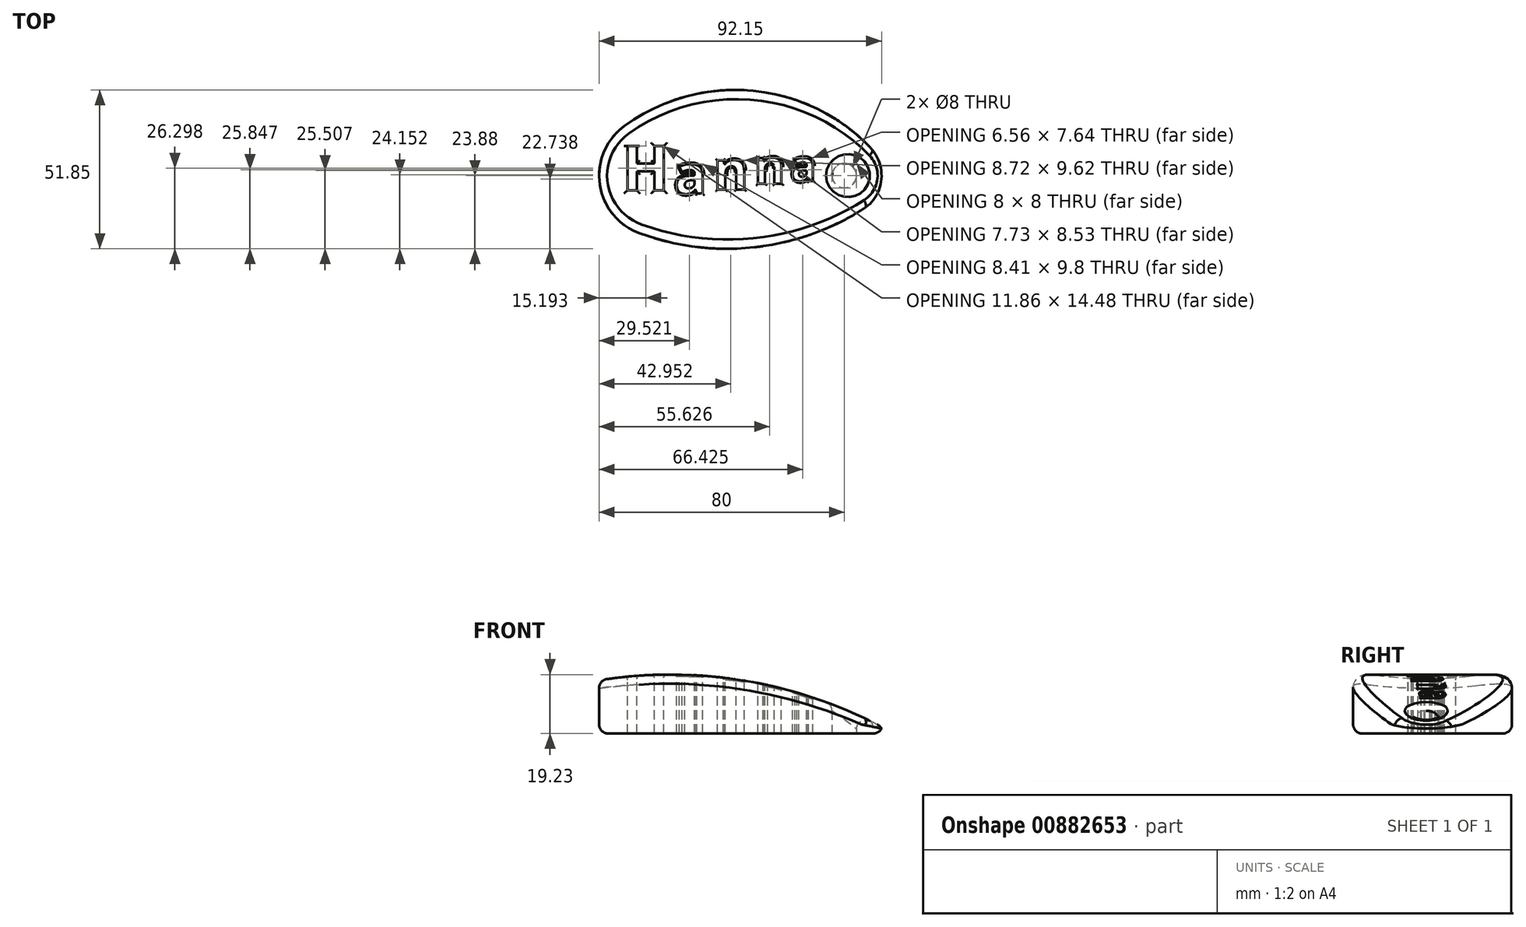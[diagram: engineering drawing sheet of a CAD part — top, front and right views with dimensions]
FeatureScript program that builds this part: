
annotation { "Feature Type Name" : "Feature", "Feature Type Description" : "" }
export const myFeature = defineFeature(function(context is Context, id is Id, definition is map)
    precondition{}
    {
        {
            var Q0;
            Q0=qCreatedBy(makeId("Top.planeOp"),FACE);
            var sketch = newSketch(context, id + "F0", { "sketchPlane" : qUnion([Q0])});
            skLineSegment(sketch, "E0", {"start": v(0, 0) * mm, "end": v(-60, 0) * mm});
            skCircle(sketch, "E1", {"center": v(0, 0) * mm, "radius": 12.5 * mm});
            skCircle(sketch, "E2", {"center": v(-60, 0) * mm, "radius": 20 * mm});
            skCircle(sketch, "E3", {"center": v(-35.63, -33.3) * mm, "radius": 61.27 * mm});
            skCircle(sketch, "E4", {"center": v(-38.3, 58.71) * mm, "radius": 82.6 * mm});
            skCircle(sketch, "E5", {"center": v(0, 0) * mm, "radius": 4 * mm});
            skSolve(sketch);
        }
        {
            var Q0;
            {var subQ0=sQuery(id+"F0.wireOp",EDGE,"E2");var subQ1=makeQuery(id+"F0.imprint","INTERSECT",VERTEX,{"derivedFrom":[sQuery(id+"F0.wireOp",EDGE,"E0"),subQ0]});Q0=makeQuery(id+"F0.imprint","IMPRINT",FACE,{"disambiguationData":[TD([[makeQuery(id+"F0.imprint","IMPRINT",EDGE,{"disambiguationData":[TD([[subQ1,-1.0]])],"derivedFrom":subQ0}),1.0]])]});}
            var Q1;
            {var subQ0=sQuery(id+"F0.wireOp",EDGE,"E1");var subQ1=sQuery(id+"F0.wireOp",EDGE,"E0");var subQ2=makeQuery(id+"F0.imprint","INTERSECT",VERTEX,{"derivedFrom":[subQ1,subQ0]});Q1=makeQuery(id+"F0.imprint","IMPRINT",FACE,{"disambiguationData":[TD([[makeQuery(id+"F0.imprint","IMPRINT",EDGE,{"disambiguationData":[TD([[subQ2,-1.0]])],"derivedFrom":subQ1}),-1.0]])]});}
            var Q2;
            Q2=makeQuery(id+"F0.imprint","IMPRINT",FACE,{"disambiguationData":[TD([[makeQuery(id+"F0.imprint","IMPRINT",EDGE,{"derivedFrom":sQuery(id+"F0.wireOp",EDGE,"E5")}),-1.0]])]});
            var Q3;
            {var subQ0=sQuery(id+"F0.wireOp",EDGE,"E1");var subQ1=sQuery(id+"F0.wireOp",EDGE,"E0");var subQ2=makeQuery(id+"F0.imprint","INTERSECT",VERTEX,{"derivedFrom":[subQ1,subQ0]});Q3=makeQuery(id+"F0.imprint","IMPRINT",FACE,{"disambiguationData":[TD([[makeQuery(id+"F0.imprint","IMPRINT",EDGE,{"disambiguationData":[TD([[subQ2,-1.0]])],"derivedFrom":subQ1}),1.0]])]});}
            extrude(context, id + "F1", {"entities" : qUnion([Q0, Q1, Q2, Q3]), "depth" : 20 * mm, "offsetDistance" : 25 * mm});
        }
        {
            var Q0;
            Q0=makeQuery(id+"F1.opExtrude","CAP_FACE",FACE,{"disambiguationData":[OSD([sQuery(id+"F0.wireOp",EDGE,"E1"),sQuery(id+"F0.wireOp",EDGE,"E2"),sQuery(id+"F0.wireOp",EDGE,"E3"),sQuery(id+"F0.wireOp",EDGE,"E4"),sQuery(id+"F0.wireOp",EDGE,"E5")])],"isStart":false});
            var sketch = newSketch(context, id + "F2", { "sketchPlane" : qUnion([Q0])});
            skText(sketch, "E6", { "text": "H", "fontName": "OpenSans-Bold.ttf"});
            skText(sketch, "E7", { "text": "a", "fontName": "OpenSans-Bold.ttf"});
            skText(sketch, "E8", { "text": "n", "fontName": "OpenSans-Bold.ttf"});
            skText(sketch, "E9", { "text": "n", "fontName": "OpenSans-Bold.ttf"});
            skText(sketch, "E10", { "text": "a", "fontName": "OpenSans-Bold.ttf"});
            const initialGuessF2  = {"E6": [-0.07256, -0.00482, 1, 0, 0.0146], "E7": [-0.05541, -0.00587, 1, 0, 0.01244], "E8": [-0.02944, -0.00264, 1, 0, 0.01105], "E9": [-0.04276, -0.00454, 1, 0, 0.01246], "E10": [-0.01742, -0.00172, 1, 0, 0.0097]};
            skSetInitialGuess(sketch, initialGuessF2);
            skSolve(sketch);
        }
        {
            var Q0;
            Q0 = qSketchRegion(id + "F2", true);
            extrude(context, id + "F3", {"entities" : qUnion([Q0]), "operationType" : NewBodyOperationType.REMOVE, "endBound" : BoundingType.THROUGH_ALL, "oppositeDirection" : true, "depth" : 25 * mm, "offsetDistance" : 25 * mm});
        }
        {
            var Q0;
            Q0=qCreatedBy(makeId("Front.planeOp"),FACE);
            cPlane(context, id + "F4", {"entities" : qUnion([Q0]), "cplaneType" : CPlaneType.OFFSET, "offset" : 40 * mm, "width" : 150 * mm, "height" : 150 * mm});
        }
        {
            var Q0;
            Q0=qCreatedBy(id+"F4.planeOp",FACE);
            var sketch = newSketch(context, id + "F5", { "sketchPlane" : qUnion([Q0])});
            skLineSegment(sketch, "E11", {"start": v(-203.83, 59.63) * mm, "end": v(87.32, 59.63) * mm});
            skLineSegment(sketch, "E12", {"start": v(87.32, 59.63) * mm, "end": v(87.32, -96.28) * mm});
            skLineSegment(sketch, "E13", {"start": v(-203.83, 59.63) * mm, "end": v(-203.83, -138.54) * mm});
            skCircle(sketch, "E14", {"center": v(-56.68, -128.28) * mm, "radius": 147.51 * mm});
            skSolve(sketch);
        }
        {
            var Q0;
            Q0=makeQuery(id+"F5.imprint","IMPRINT",FACE,{"disambiguationData":[TD([[makeQuery(id+"F5.imprint","IMPRINT",EDGE,{"derivedFrom":sQuery(id+"F5.wireOp",EDGE,"E11")}),-1.0]])]});
            extrude(context, id + "F6", {"entities" : qUnion([Q0]), "operationType" : NewBodyOperationType.REMOVE, "endBound" : BoundingType.THROUGH_ALL, "oppositeDirection" : true, "depth" : 25 * mm, "offsetDistance" : 25 * mm});
        }
        {
            var Q0;
            Q0=makeQuery(id+"F6.boolean.opBoolean","INTERSECT",EDGE,{"derivedFrom":[makeQuery(id+"F1.opExtrude","SWEPT_FACE",FACE,{"disambiguationData":[OSD([sQuery(id+"F0.wireOp",EDGE,"E4")])]}),makeQuery(id+"F6.opExtrude","SWEPT_FACE",FACE,{"disambiguationData":[OSD([sQuery(id+"F5.wireOp",EDGE,"E14")])]})]});
            var Q1;
            Q1=makeQuery(id+"F6.boolean.opBoolean","INTERSECT",EDGE,{"derivedFrom":[makeQuery(id+"F1.opExtrude","SWEPT_FACE",FACE,{"disambiguationData":[OSD([sQuery(id+"F0.wireOp",EDGE,"E5")])]}),makeQuery(id+"F6.opExtrude","SWEPT_FACE",FACE,{"disambiguationData":[OSD([sQuery(id+"F5.wireOp",EDGE,"E14")])]})]});
            var Q2;
            Q2=makeQuery(id+"F1.opExtrude","CAP_EDGE",EDGE,{"disambiguationData":[OSD([sQuery(id+"F0.wireOp",EDGE,"E3")])],"isStart":true});
            fillet(context, id + "F7", {"entities" : qUnion([Q0, Q1, Q2]), "radius" : 3 * mm, "tangentPropagation" : true, "allowEdgeOverflow" : false});
        }
        {
            var Q0;
            Q0=makeQuery(id+"F6.boolean.opBoolean","INTERSECT",EDGE,{"derivedFrom":[makeQuery(id+"F3.boolean.opBoolean","COPY",FACE,{"derivedFrom":makeQuery(id+"F3.opExtrude","SWEPT_FACE",FACE,{"disambiguationData":[OSD([sQuery(id+"F2.wireOp",EDGE,"E6.sketch_text.stroke-7")])]})}),makeQuery(id+"F6.opExtrude","SWEPT_FACE",FACE,{"disambiguationData":[OSD([sQuery(id+"F5.wireOp",EDGE,"E14")])]})]});
            var Q1;
            Q1=makeQuery(id+"F6.boolean.opBoolean","INTERSECT",EDGE,{"derivedFrom":[makeQuery(id+"F3.boolean.opBoolean","COPY",FACE,{"derivedFrom":makeQuery(id+"F3.opExtrude","SWEPT_FACE",FACE,{"disambiguationData":[OSD([sQuery(id+"F2.wireOp",EDGE,"E6.sketch_text.stroke-8")])]})}),makeQuery(id+"F6.opExtrude","SWEPT_FACE",FACE,{"disambiguationData":[OSD([sQuery(id+"F5.wireOp",EDGE,"E14")])]})]});
            var Q2;
            Q2=makeQuery(id+"F6.boolean.opBoolean","INTERSECT",EDGE,{"derivedFrom":[makeQuery(id+"F3.boolean.opBoolean","COPY",FACE,{"derivedFrom":makeQuery(id+"F3.opExtrude","SWEPT_FACE",FACE,{"disambiguationData":[OSD([sQuery(id+"F2.wireOp",EDGE,"E6.sketch_text.stroke-9")])]})}),makeQuery(id+"F6.opExtrude","SWEPT_FACE",FACE,{"disambiguationData":[OSD([sQuery(id+"F5.wireOp",EDGE,"E14")])]})]});
            var Q3;
            Q3=makeQuery(id+"F6.boolean.opBoolean","INTERSECT",EDGE,{"derivedFrom":[makeQuery(id+"F3.boolean.opBoolean","COPY",FACE,{"derivedFrom":makeQuery(id+"F3.opExtrude","SWEPT_FACE",FACE,{"disambiguationData":[OSD([sQuery(id+"F2.wireOp",EDGE,"E6.sketch_text.stroke-10")])]})}),makeQuery(id+"F6.opExtrude","SWEPT_FACE",FACE,{"disambiguationData":[OSD([sQuery(id+"F5.wireOp",EDGE,"E14")])]})]});
            var Q4;
            Q4=makeQuery(id+"F6.boolean.opBoolean","INTERSECT",EDGE,{"derivedFrom":[makeQuery(id+"F3.boolean.opBoolean","COPY",FACE,{"derivedFrom":makeQuery(id+"F3.opExtrude","SWEPT_FACE",FACE,{"disambiguationData":[OSD([sQuery(id+"F2.wireOp",EDGE,"E6.sketch_text.stroke-11")])]})}),makeQuery(id+"F6.opExtrude","SWEPT_FACE",FACE,{"disambiguationData":[OSD([sQuery(id+"F5.wireOp",EDGE,"E14")])]})]});
            var Q5;
            Q5=makeQuery(id+"F6.boolean.opBoolean","INTERSECT",EDGE,{"derivedFrom":[makeQuery(id+"F3.boolean.opBoolean","COPY",FACE,{"derivedFrom":makeQuery(id+"F3.opExtrude","SWEPT_FACE",FACE,{"disambiguationData":[OSD([sQuery(id+"F2.wireOp",EDGE,"E6.sketch_text.stroke-0")])]})}),makeQuery(id+"F6.opExtrude","SWEPT_FACE",FACE,{"disambiguationData":[OSD([sQuery(id+"F5.wireOp",EDGE,"E14")])]})]});
            var Q6;
            Q6=makeQuery(id+"F6.boolean.opBoolean","INTERSECT",EDGE,{"derivedFrom":[makeQuery(id+"F3.boolean.opBoolean","COPY",FACE,{"derivedFrom":makeQuery(id+"F3.opExtrude","SWEPT_FACE",FACE,{"disambiguationData":[OSD([sQuery(id+"F2.wireOp",EDGE,"E6.sketch_text.stroke-1")])]})}),makeQuery(id+"F6.opExtrude","SWEPT_FACE",FACE,{"disambiguationData":[OSD([sQuery(id+"F5.wireOp",EDGE,"E14")])]})]});
            var Q7;
            Q7=makeQuery(id+"F6.boolean.opBoolean","INTERSECT",EDGE,{"derivedFrom":[makeQuery(id+"F3.boolean.opBoolean","COPY",FACE,{"derivedFrom":makeQuery(id+"F3.opExtrude","SWEPT_FACE",FACE,{"disambiguationData":[OSD([sQuery(id+"F2.wireOp",EDGE,"E6.sketch_text.stroke-2")])]})}),makeQuery(id+"F6.opExtrude","SWEPT_FACE",FACE,{"disambiguationData":[OSD([sQuery(id+"F5.wireOp",EDGE,"E14")])]})]});
            var Q8;
            Q8=makeQuery(id+"F6.boolean.opBoolean","INTERSECT",EDGE,{"derivedFrom":[makeQuery(id+"F3.boolean.opBoolean","COPY",FACE,{"derivedFrom":makeQuery(id+"F3.opExtrude","SWEPT_FACE",FACE,{"disambiguationData":[OSD([sQuery(id+"F2.wireOp",EDGE,"E6.sketch_text.stroke-3")])]})}),makeQuery(id+"F6.opExtrude","SWEPT_FACE",FACE,{"disambiguationData":[OSD([sQuery(id+"F5.wireOp",EDGE,"E14")])]})]});
            var Q9;
            Q9=makeQuery(id+"F6.boolean.opBoolean","INTERSECT",EDGE,{"derivedFrom":[makeQuery(id+"F3.boolean.opBoolean","COPY",FACE,{"derivedFrom":makeQuery(id+"F3.opExtrude","SWEPT_FACE",FACE,{"disambiguationData":[OSD([sQuery(id+"F2.wireOp",EDGE,"E6.sketch_text.stroke-5")])]})}),makeQuery(id+"F6.opExtrude","SWEPT_FACE",FACE,{"disambiguationData":[OSD([sQuery(id+"F5.wireOp",EDGE,"E14")])]})]});
            var Q10;
            Q10=makeQuery(id+"F6.boolean.opBoolean","INTERSECT",EDGE,{"derivedFrom":[makeQuery(id+"F3.boolean.opBoolean","COPY",FACE,{"derivedFrom":makeQuery(id+"F3.opExtrude","SWEPT_FACE",FACE,{"disambiguationData":[OSD([sQuery(id+"F2.wireOp",EDGE,"E6.sketch_text.stroke-4")])]})}),makeQuery(id+"F6.opExtrude","SWEPT_FACE",FACE,{"disambiguationData":[OSD([sQuery(id+"F5.wireOp",EDGE,"E14")])]})]});
            fillet(context, id + "F8", {"entities" : qUnion([Q0, Q1, Q2, Q3, Q4, Q5, Q6, Q7, Q8, Q9, Q10]), "radius" : 1 * mm, "tangentPropagation" : true, "allowEdgeOverflow" : false});
        }
        {
            var Q0;
            Q0=makeQuery(id+"F6.boolean.opBoolean","INTERSECT",EDGE,{"derivedFrom":[makeQuery(id+"F3.boolean.opBoolean","COPY",FACE,{"derivedFrom":makeQuery(id+"F3.opExtrude","SWEPT_FACE",FACE,{"disambiguationData":[OSD([sQuery(id+"F2.wireOp",EDGE,"E7.sketch_text.stroke-14")])]})}),makeQuery(id+"F6.opExtrude","SWEPT_FACE",FACE,{"disambiguationData":[OSD([sQuery(id+"F5.wireOp",EDGE,"E14")])]})]});
            var Q1;
            Q1=makeQuery(id+"F6.boolean.opBoolean","INTERSECT",EDGE,{"derivedFrom":[makeQuery(id+"F3.boolean.opBoolean","COPY",FACE,{"derivedFrom":makeQuery(id+"F3.opExtrude","SWEPT_FACE",FACE,{"disambiguationData":[OSD([sQuery(id+"F2.wireOp",EDGE,"E7.sketch_text.stroke-13")])]})}),makeQuery(id+"F6.opExtrude","SWEPT_FACE",FACE,{"disambiguationData":[OSD([sQuery(id+"F5.wireOp",EDGE,"E14")])]})]});
            var Q2;
            Q2=makeQuery(id+"F6.boolean.opBoolean","INTERSECT",EDGE,{"derivedFrom":[makeQuery(id+"F3.boolean.opBoolean","COPY",FACE,{"derivedFrom":makeQuery(id+"F3.opExtrude","SWEPT_FACE",FACE,{"disambiguationData":[OSD([sQuery(id+"F2.wireOp",EDGE,"E7.sketch_text.stroke-12")])]})}),makeQuery(id+"F6.opExtrude","SWEPT_FACE",FACE,{"disambiguationData":[OSD([sQuery(id+"F5.wireOp",EDGE,"E14")])]})]});
            var Q3;
            Q3=makeQuery(id+"F6.boolean.opBoolean","INTERSECT",EDGE,{"derivedFrom":[makeQuery(id+"F3.boolean.opBoolean","COPY",FACE,{"derivedFrom":makeQuery(id+"F3.opExtrude","SWEPT_FACE",FACE,{"disambiguationData":[OSD([sQuery(id+"F2.wireOp",EDGE,"E7.sketch_text.stroke-10")])]})}),makeQuery(id+"F6.opExtrude","SWEPT_FACE",FACE,{"disambiguationData":[OSD([sQuery(id+"F5.wireOp",EDGE,"E14")])]})]});
            var Q4;
            Q4=makeQuery(id+"F6.boolean.opBoolean","INTERSECT",EDGE,{"derivedFrom":[makeQuery(id+"F3.boolean.opBoolean","COPY",FACE,{"derivedFrom":makeQuery(id+"F3.opExtrude","SWEPT_FACE",FACE,{"disambiguationData":[OSD([sQuery(id+"F2.wireOp",EDGE,"E7.sketch_text.stroke-11")])]})}),makeQuery(id+"F6.opExtrude","SWEPT_FACE",FACE,{"disambiguationData":[OSD([sQuery(id+"F5.wireOp",EDGE,"E14")])]})]});
            var Q5;
            Q5=makeQuery(id+"F6.boolean.opBoolean","INTERSECT",EDGE,{"derivedFrom":[makeQuery(id+"F3.boolean.opBoolean","COPY",FACE,{"derivedFrom":makeQuery(id+"F3.opExtrude","SWEPT_FACE",FACE,{"disambiguationData":[OSD([sQuery(id+"F2.wireOp",EDGE,"E7.sketch_text.stroke-6")])]})}),makeQuery(id+"F6.opExtrude","SWEPT_FACE",FACE,{"disambiguationData":[OSD([sQuery(id+"F5.wireOp",EDGE,"E14")])]})]});
            var Q6;
            Q6=makeQuery(id+"F6.boolean.opBoolean","INTERSECT",EDGE,{"derivedFrom":[makeQuery(id+"F3.boolean.opBoolean","COPY",FACE,{"derivedFrom":makeQuery(id+"F3.opExtrude","SWEPT_FACE",FACE,{"disambiguationData":[OSD([sQuery(id+"F2.wireOp",EDGE,"E7.sketch_text.stroke-0")])]})}),makeQuery(id+"F6.opExtrude","SWEPT_FACE",FACE,{"disambiguationData":[OSD([sQuery(id+"F5.wireOp",EDGE,"E14")])]})]});
            var Q7;
            Q7=makeQuery(id+"F6.boolean.opBoolean","INTERSECT",EDGE,{"derivedFrom":[makeQuery(id+"F3.boolean.opBoolean","COPY",FACE,{"derivedFrom":makeQuery(id+"F3.opExtrude","SWEPT_FACE",FACE,{"disambiguationData":[OSD([sQuery(id+"F2.wireOp",EDGE,"E7.sketch_text.stroke-17")])]})}),makeQuery(id+"F6.opExtrude","SWEPT_FACE",FACE,{"disambiguationData":[OSD([sQuery(id+"F5.wireOp",EDGE,"E14")])]})]});
            fillet(context, id + "F9", {"entities" : qUnion([Q0, Q1, Q2, Q3, Q4, Q5, Q6, Q7]), "radius" : 0.5 * mm, "tangentPropagation" : true, "allowEdgeOverflow" : false});
        }
        {
            var Q0;
            Q0=makeQuery(id+"F6.boolean.opBoolean","INTERSECT",EDGE,{"derivedFrom":[makeQuery(id+"F3.boolean.opBoolean","COPY",FACE,{"derivedFrom":makeQuery(id+"F3.opExtrude","SWEPT_FACE",FACE,{"disambiguationData":[OSD([sQuery(id+"F2.wireOp",EDGE,"E7.sketch_text.stroke-8")])]})}),makeQuery(id+"F6.opExtrude","SWEPT_FACE",FACE,{"disambiguationData":[OSD([sQuery(id+"F5.wireOp",EDGE,"E14")])]})]});
            var Q1;
            Q1=makeQuery(id+"F6.boolean.opBoolean","INTERSECT",EDGE,{"derivedFrom":[makeQuery(id+"F3.boolean.opBoolean","COPY",FACE,{"derivedFrom":makeQuery(id+"F3.opExtrude","SWEPT_FACE",FACE,{"disambiguationData":[OSD([sQuery(id+"F2.wireOp",EDGE,"E9.sketch_text.stroke-8")])]})}),makeQuery(id+"F6.opExtrude","SWEPT_FACE",FACE,{"disambiguationData":[OSD([sQuery(id+"F5.wireOp",EDGE,"E14")])]})]});
            var Q2;
            Q2=makeQuery(id+"F6.boolean.opBoolean","INTERSECT",EDGE,{"derivedFrom":[makeQuery(id+"F3.boolean.opBoolean","COPY",FACE,{"derivedFrom":makeQuery(id+"F3.opExtrude","SWEPT_FACE",FACE,{"disambiguationData":[OSD([sQuery(id+"F2.wireOp",EDGE,"E9.sketch_text.stroke-9")])]})}),makeQuery(id+"F6.opExtrude","SWEPT_FACE",FACE,{"disambiguationData":[OSD([sQuery(id+"F5.wireOp",EDGE,"E14")])]})]});
            var Q3;
            Q3=makeQuery(id+"F6.boolean.opBoolean","INTERSECT",EDGE,{"derivedFrom":[makeQuery(id+"F3.boolean.opBoolean","COPY",FACE,{"derivedFrom":makeQuery(id+"F3.opExtrude","SWEPT_FACE",FACE,{"disambiguationData":[OSD([sQuery(id+"F2.wireOp",EDGE,"E9.sketch_text.stroke-12")])]})}),makeQuery(id+"F6.opExtrude","SWEPT_FACE",FACE,{"disambiguationData":[OSD([sQuery(id+"F5.wireOp",EDGE,"E14")])]})]});
            var Q4;
            Q4=makeQuery(id+"F6.boolean.opBoolean","INTERSECT",EDGE,{"derivedFrom":[makeQuery(id+"F3.boolean.opBoolean","COPY",FACE,{"derivedFrom":makeQuery(id+"F3.opExtrude","SWEPT_FACE",FACE,{"disambiguationData":[OSD([sQuery(id+"F2.wireOp",EDGE,"E9.sketch_text.stroke-10")])]})}),makeQuery(id+"F6.opExtrude","SWEPT_FACE",FACE,{"disambiguationData":[OSD([sQuery(id+"F5.wireOp",EDGE,"E14")])]})]});
            var Q5;
            Q5=makeQuery(id+"F6.boolean.opBoolean","INTERSECT",EDGE,{"derivedFrom":[makeQuery(id+"F3.boolean.opBoolean","COPY",FACE,{"derivedFrom":makeQuery(id+"F3.opExtrude","SWEPT_FACE",FACE,{"disambiguationData":[OSD([sQuery(id+"F2.wireOp",EDGE,"E9.sketch_text.stroke-4")])]})}),makeQuery(id+"F6.opExtrude","SWEPT_FACE",FACE,{"disambiguationData":[OSD([sQuery(id+"F5.wireOp",EDGE,"E14")])]})]});
            var Q6;
            Q6=makeQuery(id+"F6.boolean.opBoolean","INTERSECT",EDGE,{"derivedFrom":[makeQuery(id+"F3.boolean.opBoolean","COPY",FACE,{"derivedFrom":makeQuery(id+"F3.opExtrude","SWEPT_FACE",FACE,{"disambiguationData":[OSD([sQuery(id+"F2.wireOp",EDGE,"E9.sketch_text.stroke-7")])]})}),makeQuery(id+"F6.opExtrude","SWEPT_FACE",FACE,{"disambiguationData":[OSD([sQuery(id+"F5.wireOp",EDGE,"E14")])]})]});
            var Q7;
            Q7=makeQuery(id+"F6.boolean.opBoolean","INTERSECT",EDGE,{"derivedFrom":[makeQuery(id+"F3.boolean.opBoolean","COPY",FACE,{"derivedFrom":makeQuery(id+"F3.opExtrude","SWEPT_FACE",FACE,{"disambiguationData":[OSD([sQuery(id+"F2.wireOp",EDGE,"E9.sketch_text.stroke-0")])]})}),makeQuery(id+"F6.opExtrude","SWEPT_FACE",FACE,{"disambiguationData":[OSD([sQuery(id+"F5.wireOp",EDGE,"E14")])]})]});
            fillet(context, id + "F10", {"entities" : qUnion([Q0, Q1, Q2, Q3, Q4, Q5, Q6, Q7]), "radius" : 0.5 * mm, "tangentPropagation" : true, "allowEdgeOverflow" : false});
        }
        {
            var Q0;
            Q0=makeQuery(id+"F6.boolean.opBoolean","INTERSECT",EDGE,{"derivedFrom":[makeQuery(id+"F3.boolean.opBoolean","COPY",FACE,{"derivedFrom":makeQuery(id+"F3.opExtrude","SWEPT_FACE",FACE,{"disambiguationData":[OSD([sQuery(id+"F2.wireOp",EDGE,"E8.sketch_text.stroke-14")])]})}),makeQuery(id+"F6.opExtrude","SWEPT_FACE",FACE,{"disambiguationData":[OSD([sQuery(id+"F5.wireOp",EDGE,"E14")])]})]});
            var Q1;
            Q1=makeQuery(id+"F6.boolean.opBoolean","INTERSECT",EDGE,{"derivedFrom":[makeQuery(id+"F3.boolean.opBoolean","COPY",FACE,{"derivedFrom":makeQuery(id+"F3.opExtrude","SWEPT_FACE",FACE,{"disambiguationData":[OSD([sQuery(id+"F2.wireOp",EDGE,"E8.sketch_text.stroke-9")])]})}),makeQuery(id+"F6.opExtrude","SWEPT_FACE",FACE,{"disambiguationData":[OSD([sQuery(id+"F5.wireOp",EDGE,"E14")])]})]});
            var Q2;
            Q2=makeQuery(id+"F6.boolean.opBoolean","INTERSECT",EDGE,{"derivedFrom":[makeQuery(id+"F3.boolean.opBoolean","COPY",FACE,{"derivedFrom":makeQuery(id+"F3.opExtrude","SWEPT_FACE",FACE,{"disambiguationData":[OSD([sQuery(id+"F2.wireOp",EDGE,"E8.sketch_text.stroke-10")])]})}),makeQuery(id+"F6.opExtrude","SWEPT_FACE",FACE,{"disambiguationData":[OSD([sQuery(id+"F5.wireOp",EDGE,"E14")])]})]});
            var Q3;
            Q3=makeQuery(id+"F6.boolean.opBoolean","INTERSECT",EDGE,{"derivedFrom":[makeQuery(id+"F3.boolean.opBoolean","COPY",FACE,{"derivedFrom":makeQuery(id+"F3.opExtrude","SWEPT_FACE",FACE,{"disambiguationData":[OSD([sQuery(id+"F2.wireOp",EDGE,"E8.sketch_text.stroke-8")])]})}),makeQuery(id+"F6.opExtrude","SWEPT_FACE",FACE,{"disambiguationData":[OSD([sQuery(id+"F5.wireOp",EDGE,"E14")])]})]});
            var Q4;
            Q4=makeQuery(id+"F6.boolean.opBoolean","INTERSECT",EDGE,{"derivedFrom":[makeQuery(id+"F3.boolean.opBoolean","COPY",FACE,{"derivedFrom":makeQuery(id+"F3.opExtrude","SWEPT_FACE",FACE,{"disambiguationData":[OSD([sQuery(id+"F2.wireOp",EDGE,"E8.sketch_text.stroke-6")])]})}),makeQuery(id+"F6.opExtrude","SWEPT_FACE",FACE,{"disambiguationData":[OSD([sQuery(id+"F5.wireOp",EDGE,"E14")])]})]});
            var Q5;
            Q5=makeQuery(id+"F6.boolean.opBoolean","INTERSECT",EDGE,{"derivedFrom":[makeQuery(id+"F3.boolean.opBoolean","COPY",FACE,{"derivedFrom":makeQuery(id+"F3.opExtrude","SWEPT_FACE",FACE,{"disambiguationData":[OSD([sQuery(id+"F2.wireOp",EDGE,"E8.sketch_text.stroke-7")])]})}),makeQuery(id+"F6.opExtrude","SWEPT_FACE",FACE,{"disambiguationData":[OSD([sQuery(id+"F5.wireOp",EDGE,"E14")])]})]});
            var Q6;
            Q6=makeQuery(id+"F6.boolean.opBoolean","INTERSECT",EDGE,{"derivedFrom":[makeQuery(id+"F3.boolean.opBoolean","COPY",FACE,{"derivedFrom":makeQuery(id+"F3.opExtrude","SWEPT_FACE",FACE,{"disambiguationData":[OSD([sQuery(id+"F2.wireOp",EDGE,"E8.sketch_text.stroke-0")])]})}),makeQuery(id+"F6.opExtrude","SWEPT_FACE",FACE,{"disambiguationData":[OSD([sQuery(id+"F5.wireOp",EDGE,"E14")])]})]});
            fillet(context, id + "F11", {"entities" : qUnion([Q0, Q1, Q2, Q3, Q4, Q5, Q6]), "radius" : 0.5 * mm, "tangentPropagation" : true, "allowEdgeOverflow" : false});
        }
        {
            var Q0;
            Q0=makeQuery(id+"F6.boolean.opBoolean","INTERSECT",EDGE,{"derivedFrom":[makeQuery(id+"F3.boolean.opBoolean","COPY",FACE,{"derivedFrom":makeQuery(id+"F3.opExtrude","SWEPT_FACE",FACE,{"disambiguationData":[OSD([sQuery(id+"F2.wireOp",EDGE,"E10.sketch_text.stroke-14")])]})}),makeQuery(id+"F6.opExtrude","SWEPT_FACE",FACE,{"disambiguationData":[OSD([sQuery(id+"F5.wireOp",EDGE,"E14")])]})]});
            var Q1;
            Q1=makeQuery(id+"F6.boolean.opBoolean","INTERSECT",EDGE,{"derivedFrom":[makeQuery(id+"F3.boolean.opBoolean","COPY",FACE,{"derivedFrom":makeQuery(id+"F3.opExtrude","SWEPT_FACE",FACE,{"disambiguationData":[OSD([sQuery(id+"F2.wireOp",EDGE,"E10.sketch_text.stroke-4")])]})}),makeQuery(id+"F6.opExtrude","SWEPT_FACE",FACE,{"disambiguationData":[OSD([sQuery(id+"F5.wireOp",EDGE,"E14")])]})]});
            var Q2;
            Q2=makeQuery(id+"F6.boolean.opBoolean","INTERSECT",EDGE,{"derivedFrom":[makeQuery(id+"F3.boolean.opBoolean","COPY",FACE,{"derivedFrom":makeQuery(id+"F3.opExtrude","SWEPT_FACE",FACE,{"disambiguationData":[OSD([sQuery(id+"F2.wireOp",EDGE,"E10.sketch_text.stroke-0")])]})}),makeQuery(id+"F6.opExtrude","SWEPT_FACE",FACE,{"disambiguationData":[OSD([sQuery(id+"F5.wireOp",EDGE,"E14")])]})]});
            var Q3;
            Q3=makeQuery(id+"F6.boolean.opBoolean","INTERSECT",EDGE,{"derivedFrom":[makeQuery(id+"F3.boolean.opBoolean","COPY",FACE,{"derivedFrom":makeQuery(id+"F3.opExtrude","SWEPT_FACE",FACE,{"disambiguationData":[OSD([sQuery(id+"F2.wireOp",EDGE,"E10.sketch_text.stroke-17")])]})}),makeQuery(id+"F6.opExtrude","SWEPT_FACE",FACE,{"disambiguationData":[OSD([sQuery(id+"F5.wireOp",EDGE,"E14")])]})]});
            var Q4;
            Q4=makeQuery(id+"F6.boolean.opBoolean","INTERSECT",EDGE,{"derivedFrom":[makeQuery(id+"F3.boolean.opBoolean","COPY",FACE,{"derivedFrom":makeQuery(id+"F3.opExtrude","SWEPT_FACE",FACE,{"disambiguationData":[OSD([sQuery(id+"F2.wireOp",EDGE,"E10.sketch_text.stroke-12")])]})}),makeQuery(id+"F6.opExtrude","SWEPT_FACE",FACE,{"disambiguationData":[OSD([sQuery(id+"F5.wireOp",EDGE,"E14")])]})]});
            var Q5;
            Q5=makeQuery(id+"F6.boolean.opBoolean","INTERSECT",EDGE,{"derivedFrom":[makeQuery(id+"F3.boolean.opBoolean","COPY",FACE,{"derivedFrom":makeQuery(id+"F3.opExtrude","SWEPT_FACE",FACE,{"disambiguationData":[OSD([sQuery(id+"F2.wireOp",EDGE,"E10.sketch_text.stroke-11")])]})}),makeQuery(id+"F6.opExtrude","SWEPT_FACE",FACE,{"disambiguationData":[OSD([sQuery(id+"F5.wireOp",EDGE,"E14")])]})]});
            var Q6;
            Q6=makeQuery(id+"F3.boolean.opBoolean","COPY",EDGE,{"derivedFrom":makeQuery(id+"F3.opExtrude","SWEPT_EDGE",EDGE,{"disambiguationData":[OSD([sQuery(id+"F2.wireOp",EDGE,"E10.sketch_text.stroke-18"),sQuery(id+"F2.wireOp",EDGE,"E10.sketch_text.stroke-19")])]})});
            fillet(context, id + "F12", {"entities" : qUnion([Q0, Q1, Q2, Q3, Q4, Q5, Q6]), "radius" : .5 * mm, "tangentPropagation" : true, "allowEdgeOverflow" : false});
        }
        {
            var Q0;
            Q0=makeQuery(id+"F6.boolean.opBoolean","INTERSECT",EDGE,{"derivedFrom":[makeQuery(id+"F3.boolean.opBoolean","COPY",FACE,{"derivedFrom":makeQuery(id+"F3.opExtrude","SWEPT_FACE",FACE,{"disambiguationData":[OSD([sQuery(id+"F2.wireOp",EDGE,"E10.sketch_text.stroke-8")])]})}),makeQuery(id+"F6.opExtrude","SWEPT_FACE",FACE,{"disambiguationData":[OSD([sQuery(id+"F5.wireOp",EDGE,"E14")])]})]});
            fillet(context, id + "F13", {"entities" : qUnion([Q0]), "radius" : .3 * mm, "tangentPropagation" : true, "allowEdgeOverflow" : false});
        }
    });
